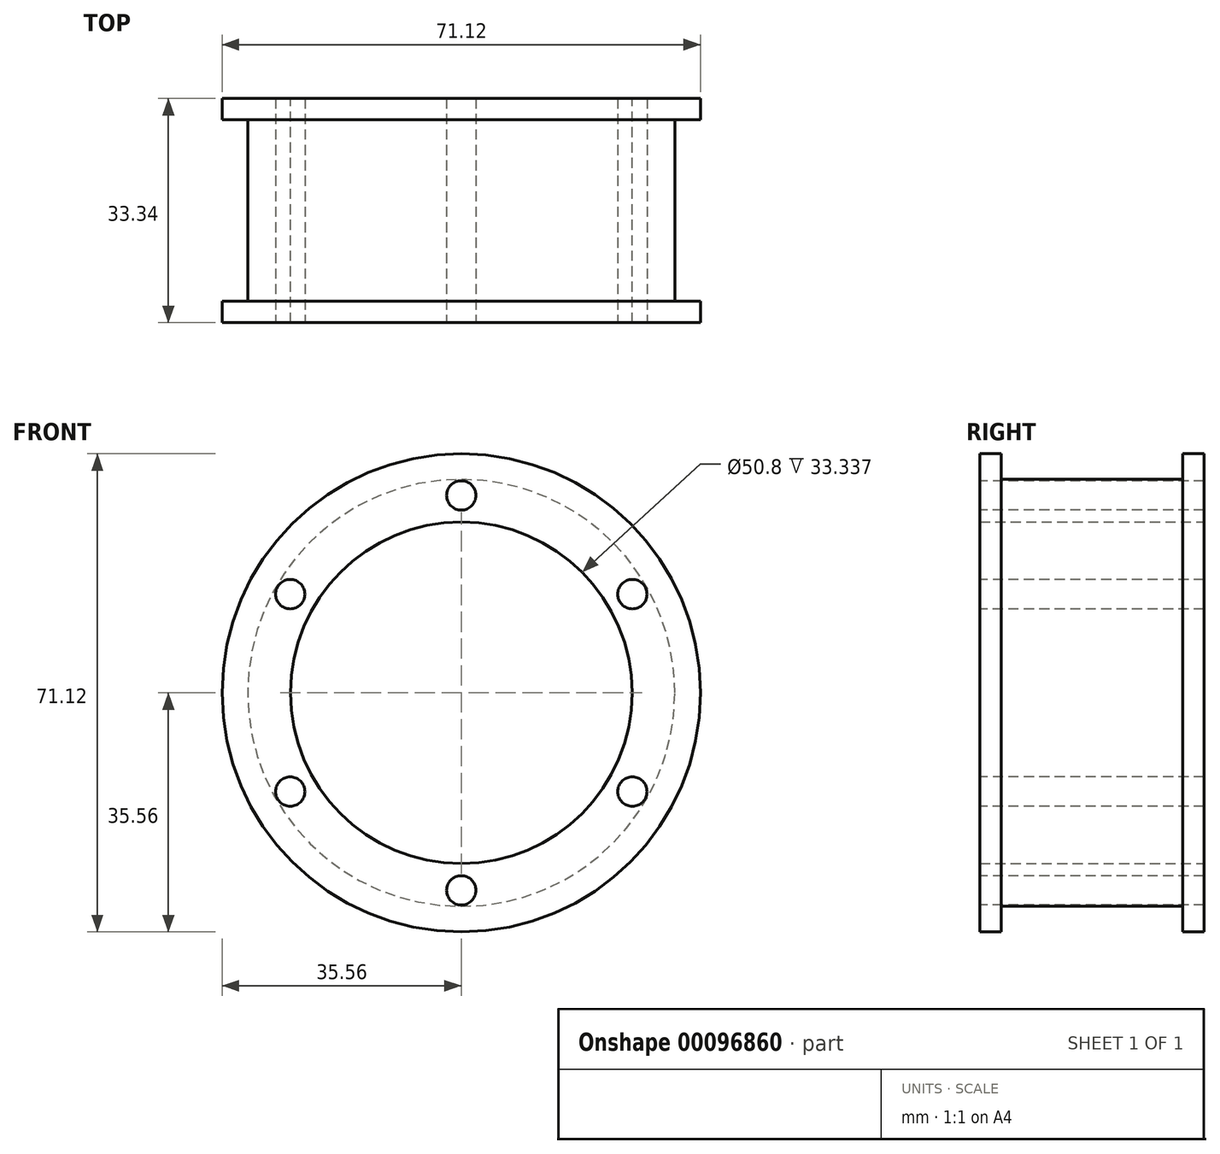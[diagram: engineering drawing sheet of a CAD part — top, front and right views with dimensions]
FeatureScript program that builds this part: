
annotation { "Feature Type Name" : "Feature", "Feature Type Description" : "" }
export const myFeature = defineFeature(function(context is Context, id is Id, definition is map)
    precondition{}
    {
        {
            var Q0;
            Q0=qCreatedBy(makeId("Front.planeOp"),FACE);
            var sketch = newSketch(context, id + "F0", { "sketchPlane" : qUnion([Q0])});
            skCircle(sketch, "E0", {"center": v(0, 0) * mm, "radius": 35.56 * mm});
            skCircle(sketch, "E1", {"center": v(0, 0) * mm, "radius": 25.4 * mm});
            skCircle(sketch, "E2", {"center": v(16, 0) * mm, "radius": 2.07 * mm});
            skSolve(sketch);
        }
        {
            var Q0;
            Q0 = qSketchRegion(id + "F0", true);
            extrude(context, id + "F1", {"entities" : qUnion([Q0]), "depth" : 3.17 * mm});
        }
        {
            var Q0;
            Q0=makeQuery(id+"F1.opExtrude","CAP_FACE",FACE,{"disambiguationData":[OSD([sQuery(id+"F0.wireOp",EDGE,"E0"),sQuery(id+"F0.wireOp",EDGE,"E1")])],"isStart":false});
            var sketch = newSketch(context, id + "F2", { "sketchPlane" : qUnion([Q0])});
            skCircle(sketch, "E3", {"center": v(0, 0) * mm, "radius": 25.4 * mm});
            skCircle(sketch, "E4", {"center": v(0, 0) * mm, "radius": 31.75 * mm});
            skSolve(sketch);
        }
        {
            var Q0;
            Q0 = qSketchRegion(id + "F2", true);
            extrude(context, id + "F3", {"entities" : qUnion([Q0]), "operationType" : NewBodyOperationType.ADD, "depth" : 26.99 * mm});
        }
        {
            var Q0;
            Q0=makeQuery(id+"F3.opExtrude","CAP_FACE",FACE,{"disambiguationData":[OSD([sQuery(id+"F2.wireOp",EDGE,"E3"),sQuery(id+"F2.wireOp",EDGE,"E4")])],"isStart":false});
            var sketch = newSketch(context, id + "F4", { "sketchPlane" : qUnion([Q0])});
            skCircle(sketch, "E5", {"center": v(0, 0) * mm, "radius": 35.56 * mm});
            skCircle(sketch, "E6", {"center": v(0, 0) * mm, "radius": 25.4 * mm});
            skSolve(sketch);
        }
        {
            var Q0;
            Q0 = qSketchRegion(id + "F4", true);
            extrude(context, id + "F5", {"entities" : qUnion([Q0]), "operationType" : NewBodyOperationType.ADD, "depth" : 3.17 * mm});
        }
        {
            var Q0;
            Q0=makeQuery(id+"F5.opExtrude","CAP_FACE",FACE,{"disambiguationData":[OSD([sQuery(id+"F4.wireOp",EDGE,"E5"),sQuery(id+"F4.wireOp",EDGE,"E6")])],"isStart":false});
            var sketch = newSketch(context, id + "F6", { "sketchPlane" : qUnion([Q0])});
            skCircle(sketch, "E7", {"center": v(0, 0) * mm, "radius": 29.37 * mm, "construction": true});
            skCircle(sketch, "E8", {"center": v(0, 29.37) * mm, "radius": 2.18 * mm});
            skCircle(sketch, "E9.1.0", {"center": v(-25.43, 14.68) * mm, "radius": 2.18 * mm});
            skCircle(sketch, "E9.2.0", {"center": v(-25.43, -14.68) * mm, "radius": 2.18 * mm});
            skCircle(sketch, "E9.3.0", {"center": v(0, -29.37) * mm, "radius": 2.18 * mm});
            skCircle(sketch, "E9.4.0", {"center": v(25.43, -14.68) * mm, "radius": 2.18 * mm});
            skCircle(sketch, "E9.5.0", {"center": v(25.43, 14.68) * mm, "radius": 2.18 * mm});
            skSolve(sketch);
        }
        {
            var Q0;
            Q0 = qSketchRegion(id + "F6", true);
            extrude(context, id + "F7", {"entities" : qUnion([Q0]), "operationType" : NewBodyOperationType.REMOVE, "endBound" : BoundingType.THROUGH_ALL, "oppositeDirection" : true, "depth" : 25.4 * mm});
        }
    });
